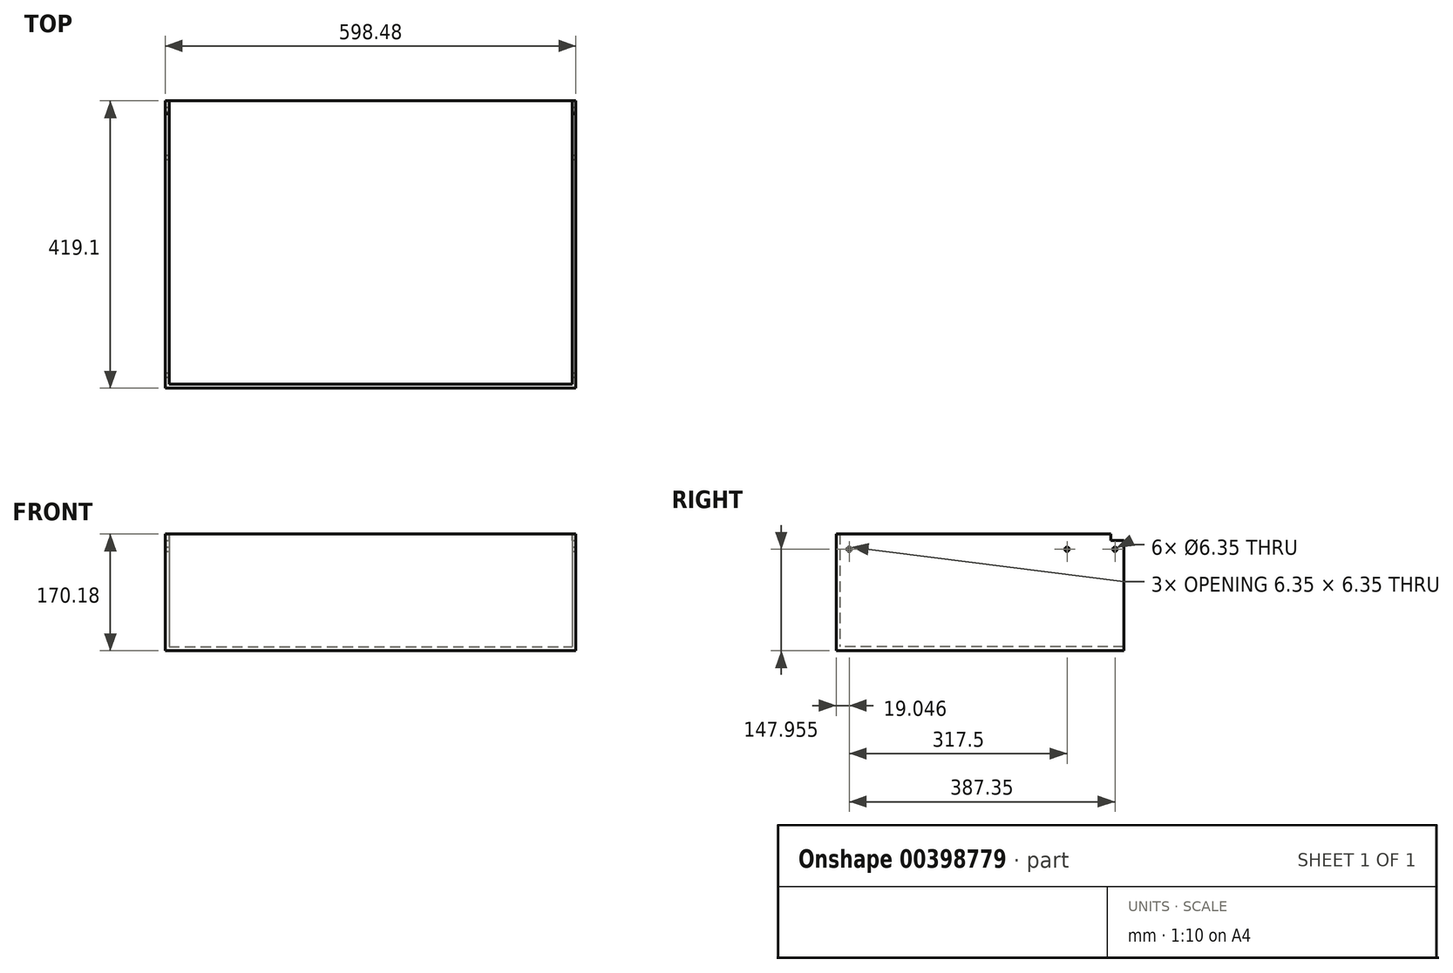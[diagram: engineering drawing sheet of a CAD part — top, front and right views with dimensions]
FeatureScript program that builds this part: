
annotation { "Feature Type Name" : "Feature", "Feature Type Description" : "" }
export const myFeature = defineFeature(function(context is Context, id is Id, definition is map)
    precondition{}
    {
        {
            var Q0;
            Q0=qCreatedBy(makeId("Front.planeOp"),FACE);
            var sketch = newSketch(context, id + "F0", { "sketchPlane" : qUnion([Q0])});
            skLineSegment(sketch, "E0.bottom", {"start": v(299.24, 85.1) * mm, "end": v(-299.24, 85.1) * mm});
            skLineSegment(sketch, "E0.top", {"start": v(299.24, -85.1) * mm, "end": v(-299.24, -85.1) * mm});
            skLineSegment(sketch, "E0.left", {"start": v(299.24, 85.1) * mm, "end": v(299.24, -85.1) * mm});
            skLineSegment(sketch, "E0.right", {"start": v(-299.24, 85.1) * mm, "end": v(-299.24, -85.1) * mm});
            skPoint(sketch, "E0.middle", {"position": v(0, 0) * mm});
            skSolve(sketch);
        }
        {
            var Q0;
            Q0=makeQuery(id+"F0.imprint","IMPRINT",FACE,{"disambiguationData":[TD([[makeQuery(id+"F0.imprint","IMPRINT",EDGE,{"derivedFrom":sQuery(id+"F0.wireOp",EDGE,"E0.bottom")}),1.0]])]});
            extrude(context, id + "F1", {"entities" : qUnion([Q0]), "endBound" : BoundingType.SYMMETRIC, "depth" : 5.6 * mm});
        }
        {
            var Q0;
            Q0=makeQuery(id+"F1.opExtrude","CAP_FACE",FACE,{"disambiguationData":[OSD([sQuery(id+"F0.wireOp",EDGE,"E0.bottom"),sQuery(id+"F0.wireOp",EDGE,"E0.top"),sQuery(id+"F0.wireOp",EDGE,"E0.left"),sQuery(id+"F0.wireOp",EDGE,"E0.right")])],"isStart":false});
            var sketch = newSketch(context, id + "F2", { "sketchPlane" : qUnion([Q0])});
            skLineSegment(sketch, "E1", {"start": v(-293.66, 85.1) * mm, "end": v(-299.24, 85.1) * mm});
            skLineSegment(sketch, "E2", {"start": v(293.66, 85.1) * mm, "end": v(299.24, 85.1) * mm});
            skLineSegment(sketch, "E3", {"start": v(-299.24, -85.1) * mm, "end": v(-293.66, -85.1) * mm});
            skLineSegment(sketch, "E4", {"start": v(-293.66, 85.1) * mm, "end": v(-293.66, -85.1) * mm});
            skLineSegment(sketch, "E5", {"start": v(293.66, 85.1) * mm, "end": v(293.66, -85.1) * mm});
            skLineSegment(sketch, "E6", {"start": v(293.66, -85.1) * mm, "end": v(299.24, -85.1) * mm});
            skLineSegment(sketch, "E7", {"start": v(299.24, -85.1) * mm, "end": v(299.24, 85.1) * mm});
            skLineSegment(sketch, "E8", {"start": v(-299.24, 85.1) * mm, "end": v(-299.24, -85.1) * mm});
            skSolve(sketch);
        }
        {
            var Q0;
            Q0=qSketchRegion(id+"F2",true);
            extrude(context, id + "F3", {"entities" : qUnion([Q0]), "operationType" : NewBodyOperationType.ADD, "oppositeDirection" : true, "depth" : 419.1 * mm});
        }
        {
            var Q0;
            Q0=makeQuery(id+"F1.opExtrude","CAP_FACE",FACE,{"disambiguationData":[OSD([sQuery(id+"F0.wireOp",EDGE,"E0.bottom"),sQuery(id+"F0.wireOp",EDGE,"E0.top"),sQuery(id+"F0.wireOp",EDGE,"E0.left"),sQuery(id+"F0.wireOp",EDGE,"E0.right")])],"isStart":true});
            var sketch = newSketch(context, id + "F4", { "sketchPlane" : qUnion([Q0])});
            skLineSegment(sketch, "E9.bottom", {"start": v(293.66, -85.1) * mm, "end": v(-293.66, -85.1) * mm});
            skLineSegment(sketch, "E9.top", {"start": v(293.66, -79.5) * mm, "end": v(-293.66, -79.5) * mm});
            skLineSegment(sketch, "E9.left", {"start": v(293.66, -85.1) * mm, "end": v(293.66, -79.5) * mm});
            skLineSegment(sketch, "E9.right", {"start": v(-293.66, -85.1) * mm, "end": v(-293.66, -79.5) * mm});
            skSolve(sketch);
        }
        {
            var Q0;
            Q0 = qSketchRegion(id + "F4", true);
            var Q1;
            Q1=makeQuery(id+"F3.opExtrude","CAP_FACE",FACE,{"disambiguationData":[OSD([sQuery(id+"F2.wireOp",EDGE,"E1"),sQuery(id+"F2.wireOp",EDGE,"E3"),sQuery(id+"F2.wireOp",EDGE,"E4"),sQuery(id+"F2.wireOp",EDGE,"E8")])],"isStart":false});
            extrude(context, id + "F5", {"entities" : qUnion([Q0]), "operationType" : NewBodyOperationType.ADD, "endBound" : BoundingType.UP_TO_SURFACE, "endBoundEntityFace" : qUnion([Q1]), "depth" : 25.4 * mm});
        }
        {
            var Q0;
            Q0=makeQuery(id+"F3.boolean.opBoolean","MERGE",FACE,{"derivedFrom":[makeQuery(id+"F1.opExtrude","SWEPT_FACE",FACE,{"disambiguationData":[OSD([sQuery(id+"F0.wireOp",EDGE,"E0.left")])]}),makeQuery(id+"F3.opExtrude","SWEPT_FACE",FACE,{"disambiguationData":[OSD([sQuery(id+"F2.wireOp",EDGE,"E7")])]})]});
            var sketch = newSketch(context, id + "F6", { "sketchPlane" : qUnion([Q0])});
            skLineSegment(sketch, "E10.bottom", {"start": v(416.3, 85.1) * mm, "end": v(397.26, 85.1) * mm});
            skLineSegment(sketch, "E10.top", {"start": v(416.3, 75.57) * mm, "end": v(397.26, 75.57) * mm});
            skLineSegment(sketch, "E10.left", {"start": v(416.3, 85.1) * mm, "end": v(416.3, 75.57) * mm});
            skLineSegment(sketch, "E10.right", {"start": v(397.26, 85.1) * mm, "end": v(397.26, 75.57) * mm});
            skSolve(sketch);
        }
        {
            var Q0;
            Q0 = qSketchRegion(id + "F6", true);
            extrude(context, id + "F7", {"entities" : qUnion([Q0]), "operationType" : NewBodyOperationType.REMOVE, "endBound" : BoundingType.THROUGH_ALL, "oppositeDirection" : true, "depth" : 25.4 * mm});
        }
        {
            var Q0;
            Q0=makeQuery(id+"F3.opExtrude","SWEPT_FACE",FACE,{"disambiguationData":[OSD([sQuery(id+"F2.wireOp",EDGE,"E4")])]});
            var sketch = newSketch(context, id + "F8", { "sketchPlane" : qUnion([Q0])});
            skLineSegment(sketch, "E11", {"start": v(333.76, -79.5) * mm, "end": v(333.76, 62.87) * mm, "construction": true});
            skLineSegment(sketch, "E12", {"start": v(333.76, 62.86) * mm, "end": v(16.26, 62.86) * mm, "construction": true});
            skLineSegment(sketch, "E13", {"start": v(333.76, 62.87) * mm, "end": v(403.6, 62.87) * mm, "construction": true});
            skLineSegment(sketch, "E14", {"start": v(403.6, 62.87) * mm, "end": v(416.3, 62.87) * mm, "construction": true});
            skCircle(sketch, "E15", {"center": v(403.6, 62.87) * mm, "radius": 3.18 * mm});
            skCircle(sketch, "E16", {"center": v(333.76, 62.87) * mm, "radius": 3.18 * mm});
            skCircle(sketch, "E17", {"center": v(16.26, 62.86) * mm, "radius": 3.18 * mm});
            skLineSegment(sketch, "E18", {"start": v(333.76, 62.87) * mm, "end": v(333.76, 85.1) * mm, "construction": true});
            skSolve(sketch);
        }
        {
            var Q0;
            Q0 = qSketchRegion(id + "F8", true);
            extrude(context, id + "F9", {"entities" : qUnion([Q0]), "operationType" : NewBodyOperationType.REMOVE, "endBound" : BoundingType.THROUGH_ALL, "oppositeDirection" : true, "depth" : 25.4 * mm, "hasSecondDirection" : true, "secondDirectionBound" : SecondDirectionBoundingType.THROUGH_ALL, "secondDirectionOppositeDirection" : false, "secondDirectionDepth" : 25.4 * mm});
        }
    });
